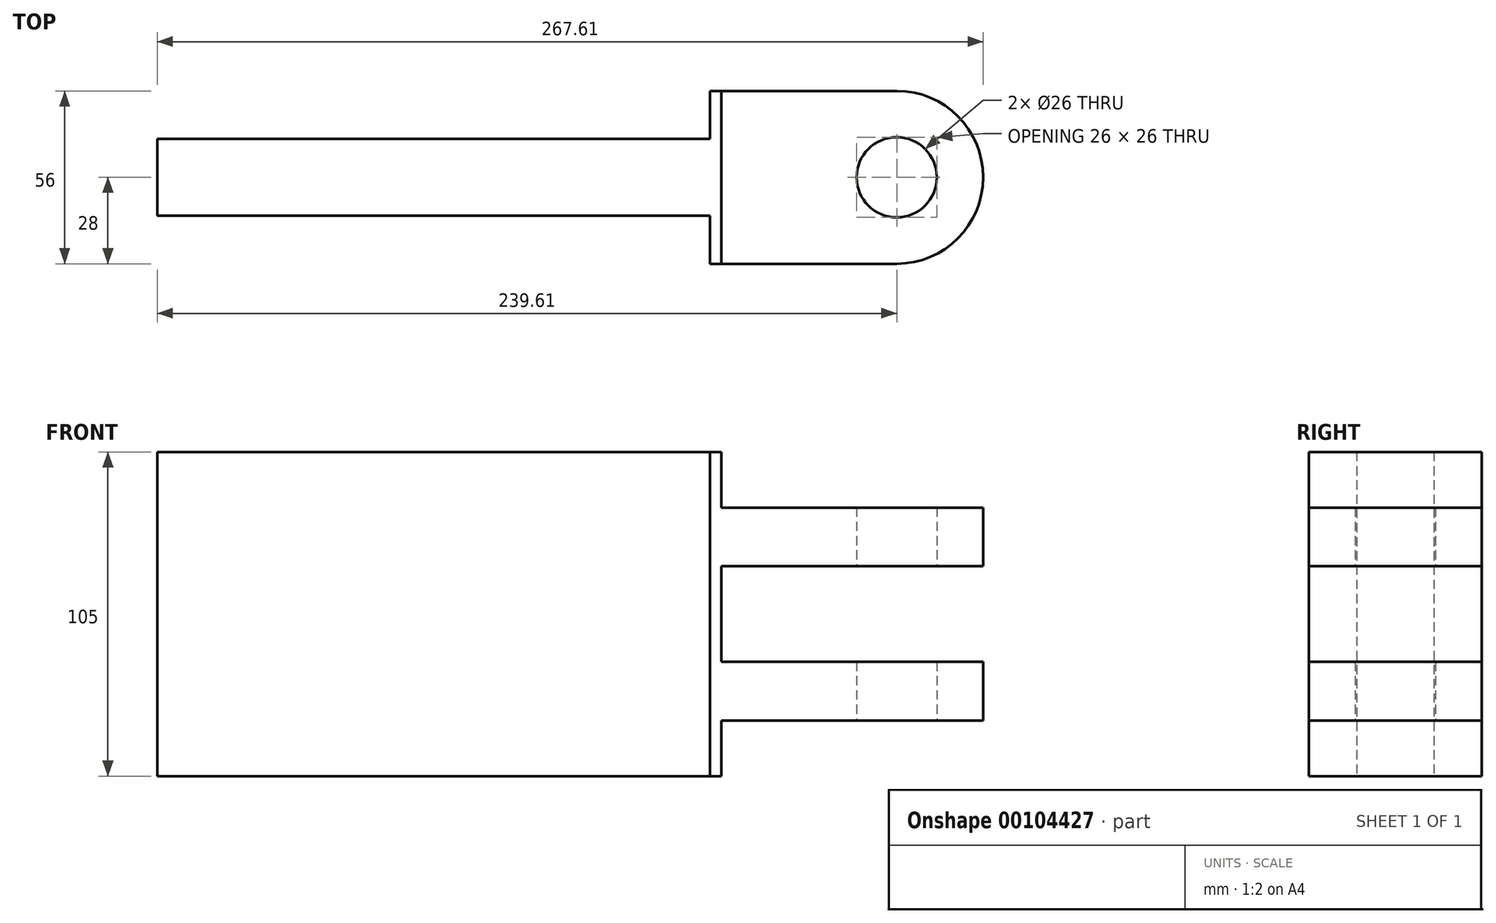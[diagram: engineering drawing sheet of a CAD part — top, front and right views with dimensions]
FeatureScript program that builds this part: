
annotation { "Feature Type Name" : "Feature", "Feature Type Description" : "" }
export const myFeature = defineFeature(function(context is Context, id is Id, definition is map)
    precondition{}
    {
        {
            var Q0;
            Q0=qCreatedBy(makeId("Top.planeOp"),FACE);
            var sketch = newSketch(context, id + "F0", { "sketchPlane" : qUnion([Q0])});
            skCircle(sketch, "E0", {"center": v(508, 0) * mm, "radius": 13 * mm});
            skLineSegment(sketch, "E1", {"start": v(508, -28) * mm, "end": v(447.43, -28) * mm});
            skLineSegment(sketch, "E2", {"start": v(447.43, -28) * mm, "end": v(447.43, -12.5) * mm});
            skLineSegment(sketch, "E3", {"start": v(447.43, -12.5) * mm, "end": v(218.83, -12.5) * mm});
            skLineSegment(sketch, "E4", {"start": v(218.83, 12.5) * mm, "end": v(447.43, 12.5) * mm});
            skLineSegment(sketch, "E5", {"start": v(447.43, 12.5) * mm, "end": v(447.43, 28) * mm});
            skLineSegment(sketch, "E6", {"start": v(447.43, 28) * mm, "end": v(508, 28) * mm});
            skArc(sketch, "E7", {"start": v(508, -28) * mm, "mid": v(536, 0) * mm, "end": v(508, 28) * mm});
            skLineSegment(sketch, "E8", {"start": v(218.83, 12.5) * mm, "end": v(218.83, -12.5) * mm});
            skSolve(sketch);
        }
        {
            var Q0;
            Q0=makeQuery(id+"F0.imprint","IMPRINT",FACE,{"disambiguationData":[TD([[makeQuery(id+"F0.imprint","IMPRINT",EDGE,{"derivedFrom":sQuery(id+"F0.wireOp",EDGE,"E0")}),-1.0]])]});
            extrude(context, id + "F1", {"entities" : qUnion([Q0]), "depth" : 105 * mm});
        }
        {
            var Q0;
            Q0=qCreatedBy(makeId("Front.planeOp"),FACE);
            var sketch = newSketch(context, id + "F2", { "sketchPlane" : qUnion([Q0])});
            skLineSegment(sketch, "E9.bottom", {"start": v(268.4, 0) * mm, "end": v(451.13, 0) * mm});
            skLineSegment(sketch, "E9.top", {"start": v(268.4, 105) * mm, "end": v(451.13, 105) * mm});
            skLineSegment(sketch, "E9.left", {"start": v(268.4, 0) * mm, "end": v(268.4, 105) * mm});
            skLineSegment(sketch, "E9.right", {"start": v(537.27, 18) * mm, "end": v(537.27, 37) * mm});
            skLineSegment(sketch, "E10", {"start": v(451.13, 105) * mm, "end": v(451.13, 87) * mm});
            skLineSegment(sketch, "E11", {"start": v(451.13, 87) * mm, "end": v(537.27, 87) * mm});
            skLineSegment(sketch, "E12", {"start": v(537.27, 68) * mm, "end": v(451.13, 68) * mm});
            skLineSegment(sketch, "E13", {"start": v(451.13, 68) * mm, "end": v(451.13, 37) * mm});
            skLineSegment(sketch, "E14", {"start": v(451.13, 37) * mm, "end": v(537.27, 37) * mm});
            skLineSegment(sketch, "E15", {"start": v(537.27, 37) * mm, "end": v(537.27, 18) * mm});
            skLineSegment(sketch, "E16", {"start": v(537.27, 18) * mm, "end": v(451.13, 18) * mm});
            skLineSegment(sketch, "E17", {"start": v(451.13, 18) * mm, "end": v(451.13, 0) * mm});
            skLineSegment(sketch, "E18.trimOffspring", {"start": v(537.27, 68) * mm, "end": v(537.27, 87) * mm});
            skSolve(sketch);
        }
        {
            var Q0;
            Q0=makeQuery(id+"F2.imprint","IMPRINT",FACE,{"disambiguationData":[TD([[makeQuery(id+"F2.imprint","IMPRINT",EDGE,{"derivedFrom":sQuery(id+"F2.wireOp",EDGE,"E9.bottom")}),1.0]])]});
            extrude(context, id + "F3", {"entities" : qUnion([Q0]), "depth" : 105 * mm, "symmetric" : true});
        }
        {
            var Q0;
            Q0=makeQuery(id+"F1.opExtrude","SWEPT_BODY",BODY,{"disambiguationData":[OSD([sQuery(id+"F0.wireOp",EDGE,"E0"),sQuery(id+"F0.wireOp",EDGE,"E1"),sQuery(id+"F0.wireOp",EDGE,"E2"),sQuery(id+"F0.wireOp",EDGE,"E3"),sQuery(id+"F0.wireOp",EDGE,"E4"),sQuery(id+"F0.wireOp",EDGE,"E5"),sQuery(id+"F0.wireOp",EDGE,"E6"),sQuery(id+"F0.wireOp",EDGE,"E7"),sQuery(id+"F0.wireOp",EDGE,"E8")])]});
            var Q1;
            Q1=makeQuery(id+"F3.opExtrude","SWEPT_BODY",BODY,{"disambiguationData":[OSD([sQuery(id+"F2.wireOp",EDGE,"E9.bottom"),sQuery(id+"F2.wireOp",EDGE,"E9.top"),sQuery(id+"F2.wireOp",EDGE,"E9.left"),sQuery(id+"F2.wireOp",EDGE,"E10"),sQuery(id+"F2.wireOp",EDGE,"E11"),sQuery(id+"F2.wireOp",EDGE,"E12"),sQuery(id+"F2.wireOp",EDGE,"E13"),sQuery(id+"F2.wireOp",EDGE,"E14"),sQuery(id+"F2.wireOp",EDGE,"E15"),sQuery(id+"F2.wireOp",EDGE,"E16"),sQuery(id+"F2.wireOp",EDGE,"E17"),sQuery(id+"F2.wireOp",EDGE,"E18.trimOffspring")])]});
            booleanBodies(context, id + "F4", {"operationType" : BooleanOperationType.INTERSECTION, "tools" : qUnion([Q0, Q1])});
        }
    });
